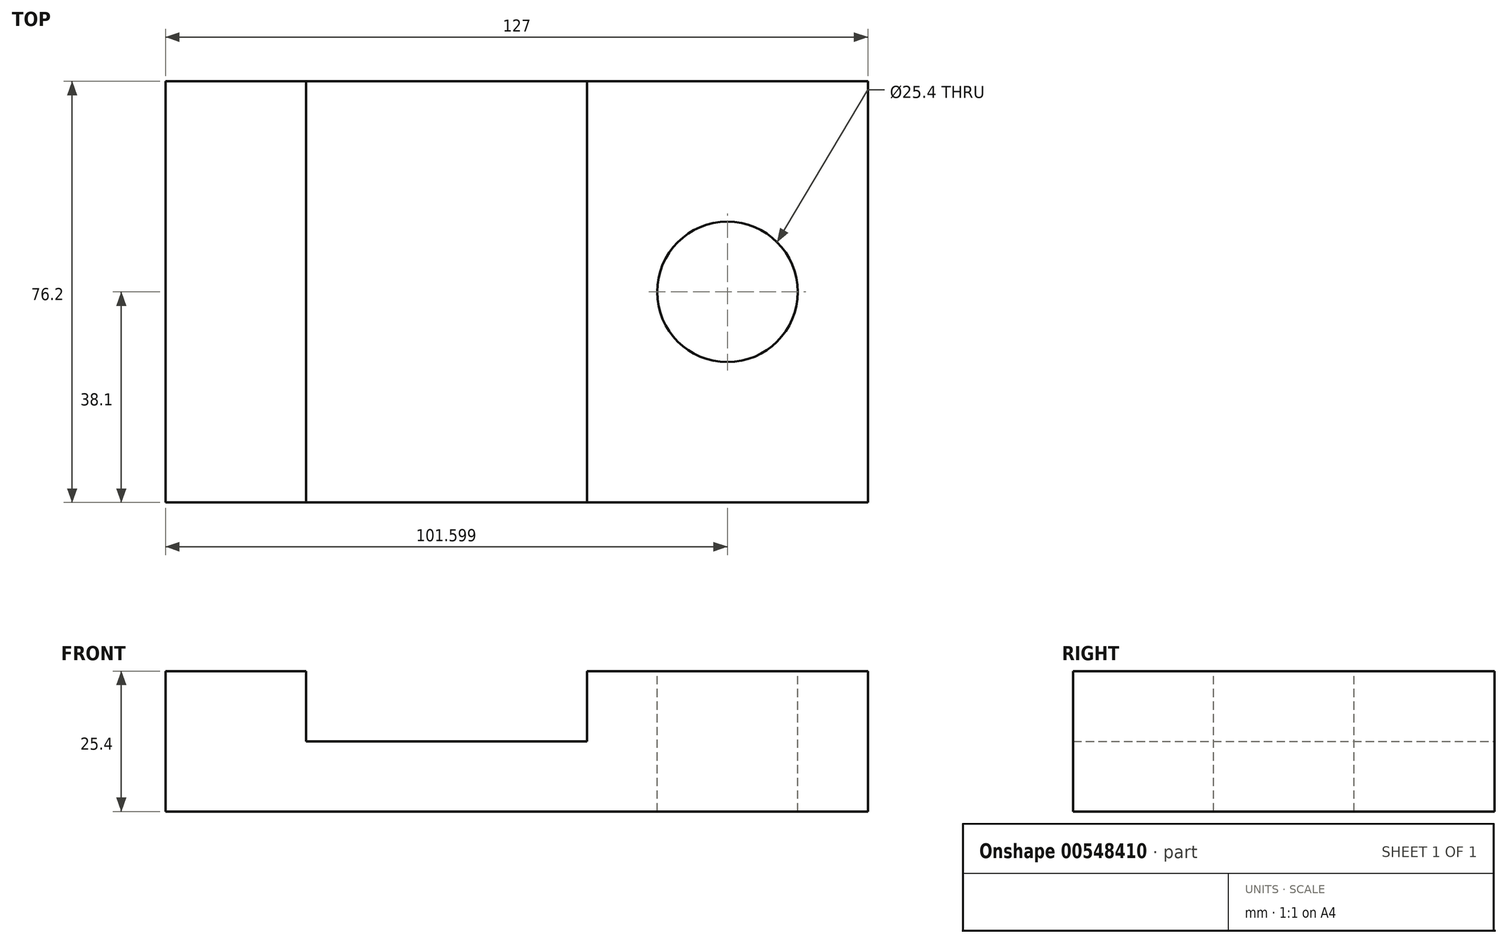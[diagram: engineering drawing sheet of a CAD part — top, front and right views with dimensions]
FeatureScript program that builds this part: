
annotation { "Feature Type Name" : "Feature", "Feature Type Description" : "" }
export const myFeature = defineFeature(function(context is Context, id is Id, definition is map)
    precondition{}
    {
        {
            var Q0;
            Q0=qCreatedBy(makeId("Front.planeOp"),FACE);
            var sketch = newSketch(context, id + "F0", { "sketchPlane" : qUnion([Q0])});
            skLineSegment(sketch, "E0", {"start": v(-64.74, 17.88) * mm, "end": v(-39.34, 17.88) * mm});
            skLineSegment(sketch, "E1", {"start": v(-39.34, 17.88) * mm, "end": v(-39.34, 5.18) * mm});
            skLineSegment(sketch, "E2", {"start": v(-39.34, 5.18) * mm, "end": v(11.46, 5.18) * mm});
            skLineSegment(sketch, "E3", {"start": v(11.46, 5.18) * mm, "end": v(11.46, 17.88) * mm});
            skLineSegment(sketch, "E4", {"start": v(11.46, 17.88) * mm, "end": v(62.26, 17.88) * mm});
            skLineSegment(sketch, "E5", {"start": v(62.26, 17.88) * mm, "end": v(62.26, -7.52) * mm});
            skLineSegment(sketch, "E6", {"start": v(62.26, -7.52) * mm, "end": v(-64.74, -7.52) * mm});
            skLineSegment(sketch, "E7", {"start": v(-64.74, -7.52) * mm, "end": v(-64.74, 17.88) * mm});
            skSolve(sketch);
        }
        {
            var Q0;
            Q0 = qSketchRegion(id + "F0", true);
            extrude(context, id + "F1", {"entities" : qUnion([Q0]), "depth" : 76.2 * mm, "offsetDistance" : 25.4 * mm});
        }
        {
            var Q0;
            Q0=makeQuery(id+"F1.opExtrude","SWEPT_FACE",FACE,{"disambiguationData":[OSD([sQuery(id+"F0.wireOp",EDGE,"E4")])]});
            var sketch = newSketch(context, id + "F2", { "sketchPlane" : qUnion([Q0])});
            skCircle(sketch, "E8", {"center": v(36.86, -38.1) * mm, "radius": 12.7 * mm});
            skSolve(sketch);
        }
        {
            var Q0;
            Q0=sQuery(id+"F2.wireOp",VERTEX,"E8.center");
            var Q1;
            Q1=makeQuery(id+"F1.opExtrude","SWEPT_BODY",BODY,{"disambiguationData":[OSD([sQuery(id+"F0.wireOp",EDGE,"E0"),sQuery(id+"F0.wireOp",EDGE,"E1"),sQuery(id+"F0.wireOp",EDGE,"E2"),sQuery(id+"F0.wireOp",EDGE,"E3"),sQuery(id+"F0.wireOp",EDGE,"E4"),sQuery(id+"F0.wireOp",EDGE,"E5"),sQuery(id+"F0.wireOp",EDGE,"E6"),sQuery(id+"F0.wireOp",EDGE,"E7")])]});
            hole(context, id + "F3", {"style" : HoleStyle.SIMPLE, "endStyle" : HoleEndStyle.THROUGH, "holeDiameter" : 25.4 * mm, "isTappedThrough" : true, "tappedDepth" : 12.7 * mm, "tapClearance" : 3, "locations" : qUnion([Q0]), "scope" : qUnion([Q1])});
        }
    });
